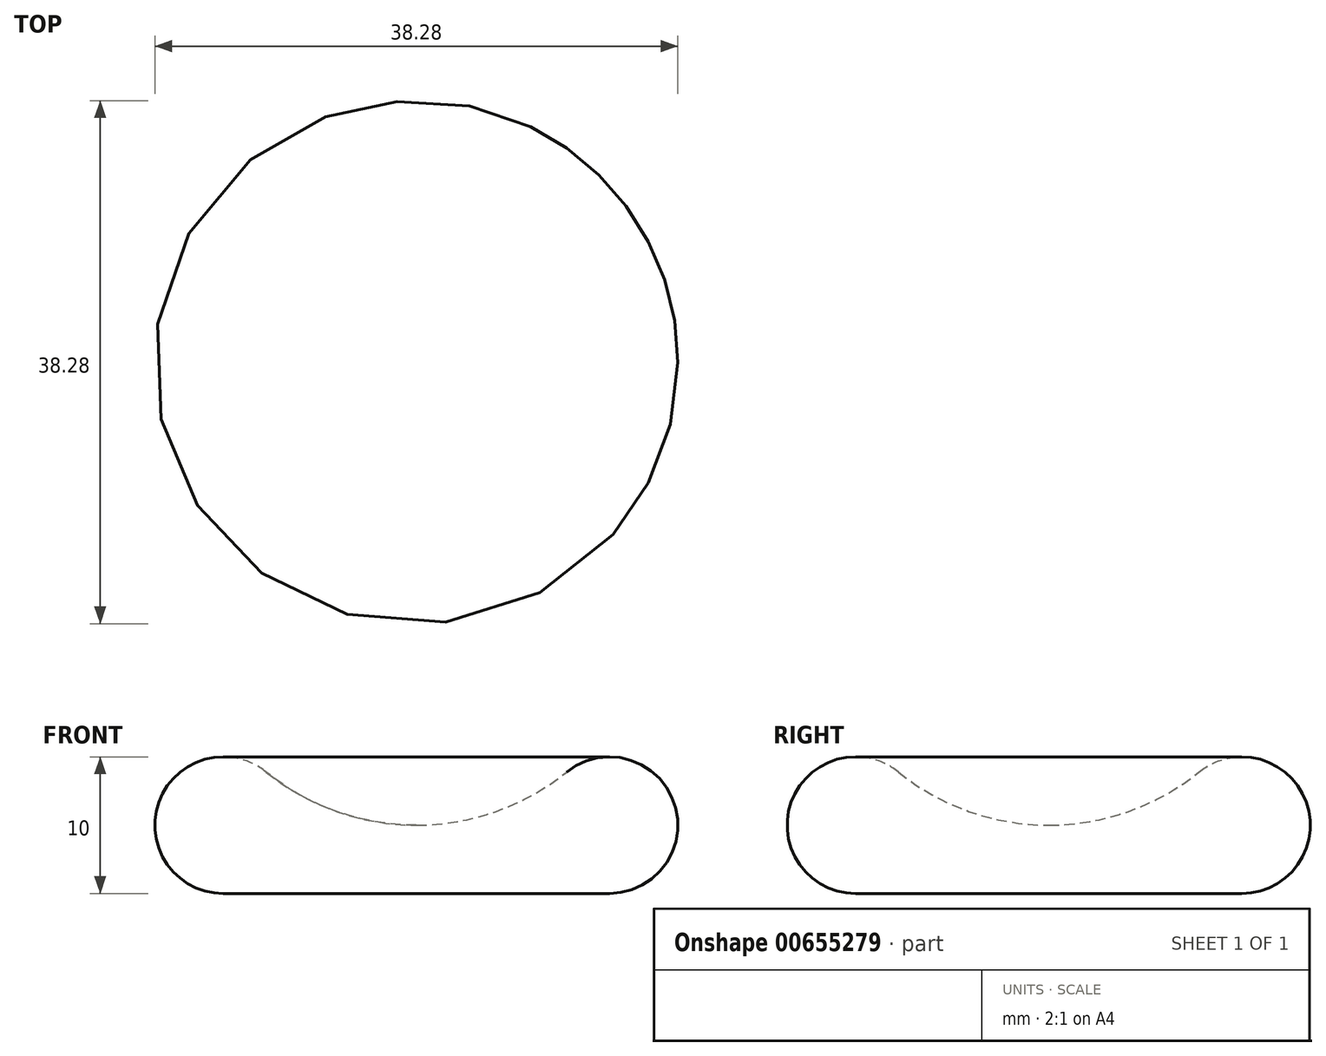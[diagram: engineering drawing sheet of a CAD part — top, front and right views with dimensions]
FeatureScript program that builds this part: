
annotation { "Feature Type Name" : "Feature", "Feature Type Description" : "" }
export const myFeature = defineFeature(function(context is Context, id is Id, definition is map)
    precondition{}
    {
        {
            var Q0;
            Q0=qCreatedBy(makeId("Front.planeOp"),FACE);
            var sketch = newSketch(context, id + "F0", { "sketchPlane" : qUnion([Q0])});
            skArc(sketch, "E0", {"start": v(-11, 8.89) * mm, "mid": v(-18.86, 6.67) * mm, "end": v(-14.14, 0) * mm});
            skArc(sketch, "E1", {"start": v(-11, 8.89) * mm, "mid": v(-5.83, 6) * mm, "end": v(0, 5) * mm});
            skLineSegment(sketch, "E2", {"start": v(-14.14, 0) * mm, "end": v(0, 0) * mm});
            skLineSegment(sketch, "E3", {"start": v(0, 5) * mm, "end": v(0, 0) * mm});
            skSolve(sketch);
        }
        {
            var Q0;
            Q0=makeQuery(id+"F0.imprint","IMPRINT",FACE,{"disambiguationData":[TD([[makeQuery(id+"F0.imprint","IMPRINT",EDGE,{"derivedFrom":sQuery(id+"F0.wireOp",EDGE,"E0")}),1.0]])]});
            var Q1;
            Q1=sQuery(id+"F0.wireOp",EDGE,"E3");
            revolve(context, id + "F1", {"entities" : qUnion([Q0]), "axis" : qUnion([Q1]), "revolveType" : RevolveType.FULL});
        }
        {
            var Q0;
            Q0=qCreatedBy(makeId("Top.planeOp"),FACE);
            cPlane(context, id + "F2", {"entities" : qUnion([Q0]), "cplaneType" : CPlaneType.OFFSET, "offset" : 10 * mm, "width" : 150 * mm, "height" : 150 * mm});
        }
    });
